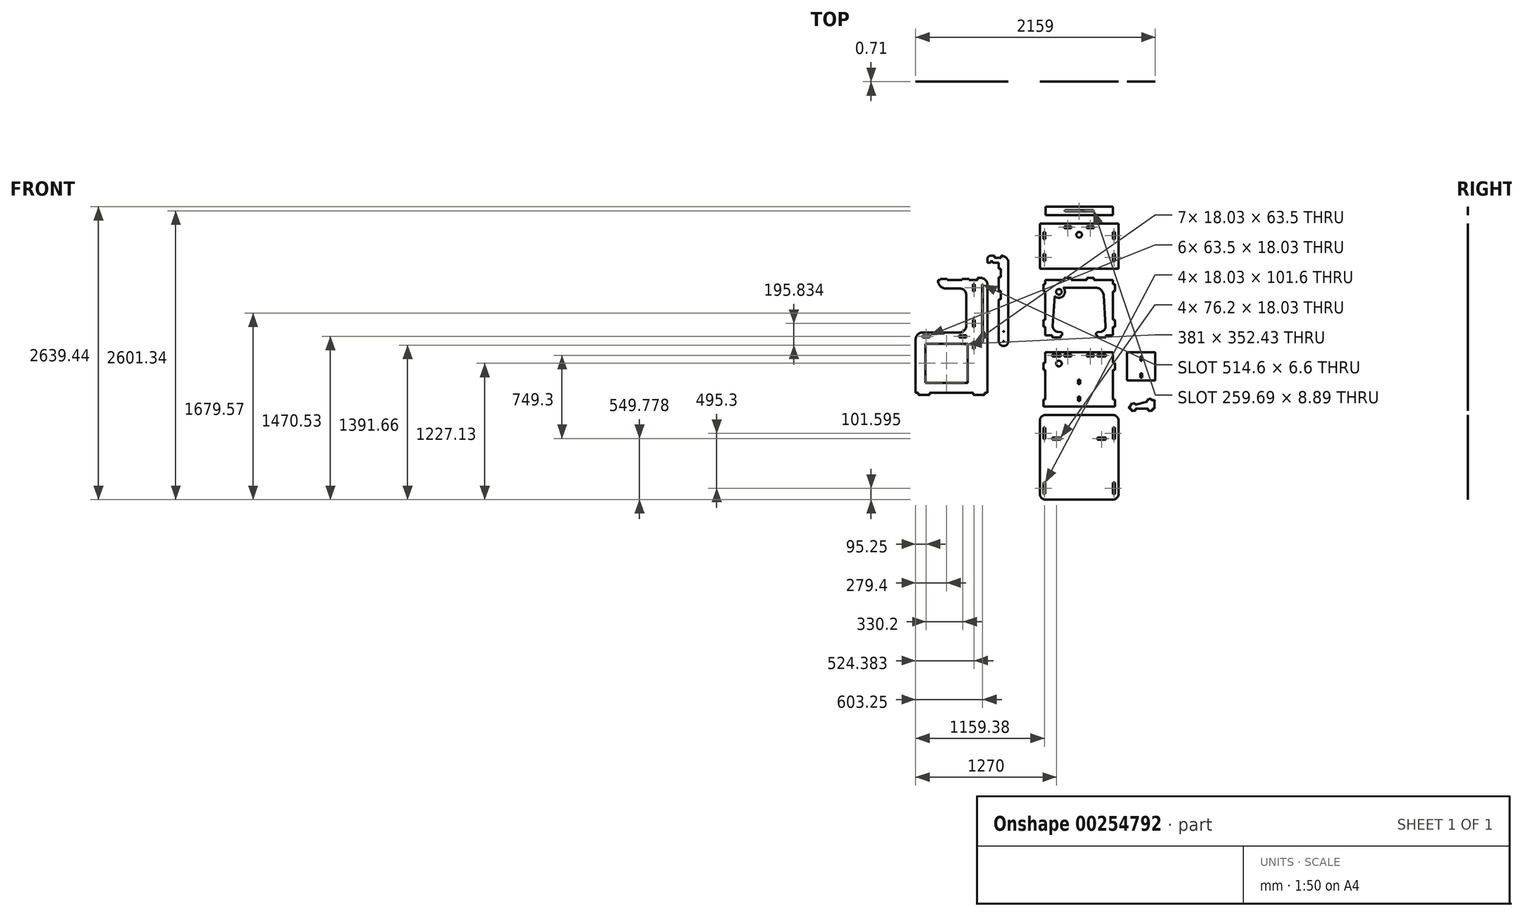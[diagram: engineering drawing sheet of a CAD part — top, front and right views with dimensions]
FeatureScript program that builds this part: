
annotation { "Feature Type Name" : "Feature", "Feature Type Description" : "" }
export const myFeature = defineFeature(function(context is Context, id is Id, definition is map)
    precondition{}
    {
        {
            assignVariable(context, id + "F0", {"name" : "ply34", "anyValue" : .71});
        }
        {
            var Q0;
            Q0=qCreatedBy(makeId("Front.planeOp"),FACE);
            var sketch = newSketch(context, id + "F1", { "sketchPlane" : qUnion([Q0])});
            skLineSegment(sketch, "E0.bottom", {"start": v(-279.4, 635) * mm, "end": v(279.4, 635) * mm, "construction": true});
            skLineSegment(sketch, "E0.top", {"start": v(-279.4, -635) * mm, "end": v(279.4, -635) * mm});
            skPoint(sketch, "E0.middle", {"position": v(0, 0) * mm});
            skLineSegment(sketch, "E1", {"start": v(0, 869.95) * mm, "end": v(0, 400.05) * mm, "construction": true});
            skPoint(sketch, "E1.endSnap0", {"position": v(0, 635) * mm});
            skLineSegment(sketch, "E2", {"start": v(279.4, -635) * mm, "end": v(279.4, -482.6) * mm, "construction": true});
            skLineSegment(sketch, "E3", {"start": v(279.4, 400.05) * mm, "end": v(304.8, 400.05) * mm});
            skLineSegment(sketch, "E4", {"start": v(368.3, 336.55) * mm, "end": v(368.3, -635) * mm});
            skLineSegment(sketch, "E5", {"start": v(323.85, -234.95) * mm, "end": v(323.85, -234.95) * mm});
            skLineSegment(sketch, "E6", {"start": v(279.4, 382.02) * mm, "end": v(-76.2, 382.02) * mm});
            skLineSegment(sketch, "E7", {"start": v(-76.2, 382.02) * mm, "end": v(-76.2, 369.32) * mm});
            skLineSegment(sketch, "E8", {"start": v(-12.7, 305.82) * mm, "end": v(114.3, 305.82) * mm});
            skLineSegment(sketch, "E9", {"start": v(177.8, 242.32) * mm, "end": v(177.8, -28.57) * mm});
            skLineSegment(sketch, "E10", {"start": v(114.3, -92.07) * mm, "end": v(-215.9, -92.08) * mm});
            skPoint(sketch, "E11", {"position": v(279.4, -117.47) * mm});
            skLineSegment(sketch, "E12", {"start": v(-279.4, -155.58) * mm, "end": v(-279.4, -635) * mm});
            skLineSegment(sketch, "E13", {"start": v(-57.15, 382.02) * mm, "end": v(-57.15, 391.03) * mm});
            skLineSegment(sketch, "E14", {"start": v(-57.15, 391.03) * mm, "end": v(6.35, 391.03) * mm});
            skLineSegment(sketch, "E15", {"start": v(6.35, 391.03) * mm, "end": v(6.35, 382.02) * mm});
            skLineSegment(sketch, "E16", {"start": v(139.7, 382.02) * mm, "end": v(139.7, 391.03) * mm});
            skLineSegment(sketch, "E17", {"start": v(139.7, 391.03) * mm, "end": v(203.2, 391.03) * mm});
            skLineSegment(sketch, "E18", {"start": v(203.2, 391.03) * mm, "end": v(203.2, 382.02) * mm});
            skPoint(sketch, "E19.visualSharp", {"position": v(-76.2, 305.82) * mm});
            skArc(sketch, "E19.filletArc", {"start": v(-76.2, 369.32) * mm, "mid": v(-57.6, 324.41) * mm, "end": v(-12.7, 305.82) * mm});
            skPoint(sketch, "E20.visualSharp", {"position": v(177.8, 305.82) * mm});
            skArc(sketch, "E20.filletArc", {"start": v(177.8, 242.32) * mm, "mid": v(159.2, 287.22) * mm, "end": v(114.3, 305.82) * mm});
            skPoint(sketch, "E21.visualSharp", {"position": v(177.8, -92.07) * mm});
            skArc(sketch, "E21.filletArc", {"start": v(114.3, -92.08) * mm, "mid": v(159.2, -73.48) * mm, "end": v(177.8, -28.57) * mm});
            skPoint(sketch, "E22.visualSharp", {"position": v(-279.4, -92.08) * mm});
            skArc(sketch, "E22.filletArc", {"start": v(-215.9, -92.08) * mm, "mid": v(-260.8, -110.67) * mm, "end": v(-279.4, -155.58) * mm});
            skPoint(sketch, "E23.visualSharp", {"position": v(368.3, 400.05) * mm});
            skArc(sketch, "E23.filletArc", {"start": v(368.3, 336.55) * mm, "mid": v(349.7, 381.45) * mm, "end": v(304.8, 400.05) * mm});
            skLineSegment(sketch, "E24", {"start": v(279.4, -234.95) * mm, "end": v(279.4, 400.05) * mm, "construction": true});
            skLineSegment(sketch, "E25", {"start": v(279.4, 400.05) * mm, "end": v(279.4, 382.02) * mm});
            skLineSegment(sketch, "E26.bottom", {"start": v(-215.9, -117.47) * mm, "end": v(-152.4, -117.47) * mm});
            skLineSegment(sketch, "E26.top", {"start": v(-215.9, -135.5) * mm, "end": v(-152.4, -135.5) * mm});
            skLineSegment(sketch, "E26.left", {"start": v(-215.9, -117.47) * mm, "end": v(-215.9, -135.5) * mm});
            skLineSegment(sketch, "E26.right", {"start": v(-152.4, -117.47) * mm, "end": v(-152.4, -135.5) * mm});
            skLineSegment(sketch, "E27.bottom", {"start": v(177.8, -117.47) * mm, "end": v(114.3, -117.47) * mm});
            skLineSegment(sketch, "E27.top", {"start": v(177.8, -135.5) * mm, "end": v(114.3, -135.5) * mm});
            skLineSegment(sketch, "E27.left", {"start": v(177.8, -117.48) * mm, "end": v(177.8, -135.5) * mm});
            skLineSegment(sketch, "E27.right", {"start": v(114.3, -117.48) * mm, "end": v(114.3, -135.5) * mm});
            skLineSegment(sketch, "E28", {"start": v(279.4, 82.55) * mm, "end": v(368.3, 82.55) * mm, "construction": true});
            skLineSegment(sketch, "E29", {"start": v(323.85, 336.55) * mm, "end": v(323.85, -171.45) * mm});
            skPoint(sketch, "E29.startSnap0", {"position": v(323.85, 82.55) * mm});
            skPoint(sketch, "E30.visualSharp", {"position": v(368.3, -234.95) * mm});
            skPoint(sketch, "E31.visualSharp", {"position": v(279.4, -234.95) * mm});
            skArc(sketch, "E32.0.startCap", {"start": v(320.55, 336.55) * mm, "mid": v(323.85, 339.85) * mm, "end": v(327.15, 336.55) * mm});
            skArc(sketch, "E32.0.endCap", {"start": v(327.15, -171.45) * mm, "mid": v(323.85, -174.75) * mm, "end": v(320.55, -171.45) * mm});
            skLineSegment(sketch, "E32.0.left", {"start": v(327.15, 336.55) * mm, "end": v(327.15, -171.45) * mm});
            skLineSegment(sketch, "E32.0.right", {"start": v(320.55, 336.55) * mm, "end": v(320.55, -171.45) * mm});
            skLineSegment(sketch, "E33.0", {"start": v(190.5, -546.1) * mm, "end": v(190.5, -193.68) * mm});
            skLineSegment(sketch, "E33.1", {"start": v(-190.5, -546.1) * mm, "end": v(190.5, -546.1) * mm});
            skLineSegment(sketch, "E33.2", {"start": v(-190.5, -193.68) * mm, "end": v(-190.5, -546.1) * mm});
            skLineSegment(sketch, "E34", {"start": v(-190.5, -193.68) * mm, "end": v(190.5, -193.67) * mm});
            skLineSegment(sketch, "E35.bottom", {"start": v(254, 343.92) * mm, "end": v(235.97, 343.92) * mm});
            skLineSegment(sketch, "E35.top", {"start": v(254, 280.42) * mm, "end": v(235.97, 280.42) * mm});
            skLineSegment(sketch, "E35.left", {"start": v(254, 343.92) * mm, "end": v(254, 280.42) * mm});
            skLineSegment(sketch, "E35.right", {"start": v(235.97, 343.92) * mm, "end": v(235.97, 280.42) * mm});
            skLineSegment(sketch, "E36.bottom", {"start": v(235.97, 22.23) * mm, "end": v(254, 22.23) * mm});
            skLineSegment(sketch, "E36.top", {"start": v(235.97, -41.27) * mm, "end": v(254, -41.27) * mm});
            skLineSegment(sketch, "E36.left", {"start": v(235.97, 22.22) * mm, "end": v(235.97, -41.28) * mm});
            skLineSegment(sketch, "E36.right", {"start": v(254, 22.22) * mm, "end": v(254, -41.28) * mm});
            skLineSegment(sketch, "E37", {"start": v(889, -117.47) * mm, "end": v(1498.6, -117.47) * mm, "construction": true});
            skLineSegment(sketch, "E38", {"start": v(1041.4, -117.47) * mm, "end": v(1041.4, -103.09) * mm});
            skLineSegment(sketch, "E39", {"start": v(1193.8, -117.47) * mm, "end": v(1193.8, 9.53) * mm, "construction": true});
            skLineSegment(sketch, "E40", {"start": v(1030.5, -90.52) * mm, "end": v(999.05, -86.03) * mm});
            skLineSegment(sketch, "E41", {"start": v(955.54, -32.45) * mm, "end": v(973.28, 240.9) * mm});
            skPoint(sketch, "E41.endSnap0", {"position": v(254, 312.17) * mm});
            skPoint(sketch, "E42.visualSharp", {"position": v(1041.4, -92.07) * mm});
            skArc(sketch, "E42.filletArc", {"start": v(1041.4, -103.09) * mm, "mid": v(1038.3, -94.77) * mm, "end": v(1030.5, -90.52) * mm});
            skPoint(sketch, "E43.visualSharp", {"position": v(952.5, -79.37) * mm});
            skArc(sketch, "E43.filletArc", {"start": v(955.54, -32.45) * mm, "mid": v(966.8, -67.76) * mm, "end": v(999.05, -86.03) * mm});
            skLineSegment(sketch, "E44", {"start": v(889, -117.47) * mm, "end": v(889, 382.02) * mm});
            skLineSegment(sketch, "E45", {"start": v(1041.4, -117.47) * mm, "end": v(889, -117.47) * mm});
            skLineSegment(sketch, "E46", {"start": v(1028.7, -117.47) * mm, "end": v(1028.7, -135.5) * mm});
            skLineSegment(sketch, "E47", {"start": v(1028.7, -135.5) * mm, "end": v(952.5, -135.5) * mm});
            skLineSegment(sketch, "E48", {"start": v(952.5, -135.5) * mm, "end": v(952.5, -117.47) * mm});
            skLineSegment(sketch, "E49.MirrorCS", {"start": v(1432.06, -32.45) * mm, "end": v(1414.32, 240.9) * mm});
            skLineSegment(sketch, "E50.MirrorCS", {"start": v(1498.6, -117.47) * mm, "end": v(1498.6, 382.02) * mm});
            skArc(sketch, "E51.MirrorCS", {"start": v(1432.06, -32.45) * mm, "mid": v(1420.8, -67.76) * mm, "end": v(1388.55, -86.03) * mm});
            skLineSegment(sketch, "E52.MirrorCS", {"start": v(1357.1, -90.52) * mm, "end": v(1388.55, -86.03) * mm});
            skArc(sketch, "E53.MirrorCS", {"start": v(1346.2, -103.09) * mm, "mid": v(1349.3, -94.77) * mm, "end": v(1357.1, -90.52) * mm});
            skLineSegment(sketch, "E54.MirrorCS", {"start": v(1346.2, -117.47) * mm, "end": v(1346.2, -103.09) * mm});
            skLineSegment(sketch, "E55.MirrorCS", {"start": v(1435.1, -135.5) * mm, "end": v(1435.1, -117.47) * mm});
            skLineSegment(sketch, "E56.MirrorCS", {"start": v(1358.9, -135.5) * mm, "end": v(1435.1, -135.5) * mm});
            skLineSegment(sketch, "E57.MirrorCS", {"start": v(1346.2, -117.48) * mm, "end": v(1498.6, -117.48) * mm});
            skLineSegment(sketch, "E58.MirrorCS", {"start": v(1358.9, -117.47) * mm, "end": v(1358.9, -135.5) * mm});
            skLineSegment(sketch, "E59", {"start": v(1049.32, 312.17) * mm, "end": v(1338.28, 312.17) * mm});
            skPoint(sketch, "E60.visualSharp", {"position": v(977.9, 312.17) * mm});
            skArc(sketch, "E60.filletArc", {"start": v(1049.32, 312.17) * mm, "mid": v(997.2, 291.56) * mm, "end": v(973.28, 240.9) * mm});
            skPoint(sketch, "E61.visualSharp", {"position": v(1409.7, 312.17) * mm});
            skArc(sketch, "E61.filletArc", {"start": v(1414.32, 240.9) * mm, "mid": v(1390.4, 291.56) * mm, "end": v(1338.28, 312.17) * mm});
            skLineSegment(sketch, "E62", {"start": v(889, 382.02) * mm, "end": v(1498.6, 382.02) * mm});
            skLineSegment(sketch, "E63", {"start": v(1060.45, 382.02) * mm, "end": v(1060.45, 400.05) * mm});
            skLineSegment(sketch, "E64", {"start": v(1060.45, 400.05) * mm, "end": v(1123.95, 400.05) * mm});
            skLineSegment(sketch, "E65", {"start": v(1123.95, 400.05) * mm, "end": v(1123.95, 382.02) * mm});
            skLineSegment(sketch, "E66", {"start": v(889, 343.92) * mm, "end": v(870.97, 343.92) * mm});
            skLineSegment(sketch, "E67", {"start": v(870.97, 343.92) * mm, "end": v(870.97, 280.42) * mm});
            skLineSegment(sketch, "E68", {"start": v(870.97, 280.42) * mm, "end": v(889, 280.42) * mm});
            skLineSegment(sketch, "E69", {"start": v(889, -41.27) * mm, "end": v(870.97, -41.27) * mm});
            skLineSegment(sketch, "E70", {"start": v(870.97, -41.27) * mm, "end": v(870.97, 22.23) * mm});
            skLineSegment(sketch, "E71", {"start": v(870.97, 22.22) * mm, "end": v(889, 22.22) * mm});
            skLineSegment(sketch, "E72.MirrorCS", {"start": v(1516.63, 22.23) * mm, "end": v(1498.6, 22.23) * mm});
            skLineSegment(sketch, "E73.MirrorCS", {"start": v(1498.6, -41.28) * mm, "end": v(1516.63, -41.28) * mm});
            skLineSegment(sketch, "E74.MirrorCS", {"start": v(1498.6, 343.92) * mm, "end": v(1516.63, 343.92) * mm});
            skLineSegment(sketch, "E75.MirrorCS", {"start": v(1516.63, 280.42) * mm, "end": v(1498.6, 280.42) * mm});
            skLineSegment(sketch, "E76.MirrorCS", {"start": v(1516.63, -41.27) * mm, "end": v(1516.63, 22.23) * mm});
            skLineSegment(sketch, "E77.MirrorCS", {"start": v(1516.63, 343.92) * mm, "end": v(1516.63, 280.42) * mm});
            skLineSegment(sketch, "E78.bottom", {"start": v(1498.6, -269.88) * mm, "end": v(889, -269.87) * mm});
            skLineSegment(sketch, "E78.top", {"start": v(1498.6, -758.83) * mm, "end": v(889, -758.83) * mm});
            skLineSegment(sketch, "E78.left", {"start": v(1498.6, -269.87) * mm, "end": v(1498.6, -758.83) * mm});
            skLineSegment(sketch, "E78.right", {"start": v(889, -269.87) * mm, "end": v(889, -758.83) * mm});
            skLineSegment(sketch, "E79", {"start": v(889, -365.12) * mm, "end": v(870.97, -365.12) * mm});
            skLineSegment(sketch, "E80", {"start": v(870.97, -365.12) * mm, "end": v(870.97, -428.63) * mm});
            skLineSegment(sketch, "E81", {"start": v(870.97, -428.63) * mm, "end": v(889, -428.63) * mm});
            skLineSegment(sketch, "E82", {"start": v(889, -695.32) * mm, "end": v(870.97, -695.32) * mm});
            skLineSegment(sketch, "E83", {"start": v(870.97, -695.32) * mm, "end": v(870.97, -758.82) * mm});
            skLineSegment(sketch, "E84", {"start": v(870.97, -758.82) * mm, "end": v(889, -758.82) * mm});
            skLineSegment(sketch, "E85.MirrorCS", {"start": v(1516.63, -758.82) * mm, "end": v(1498.6, -758.82) * mm});
            skLineSegment(sketch, "E86.MirrorCS", {"start": v(1498.6, -695.33) * mm, "end": v(1516.63, -695.33) * mm});
            skLineSegment(sketch, "E87.MirrorCS", {"start": v(1516.63, -428.62) * mm, "end": v(1498.6, -428.62) * mm});
            skLineSegment(sketch, "E88.MirrorCS", {"start": v(1498.6, -365.12) * mm, "end": v(1516.63, -365.12) * mm});
            skLineSegment(sketch, "E89.MirrorCS", {"start": v(1516.63, -695.32) * mm, "end": v(1516.63, -758.82) * mm});
            skLineSegment(sketch, "E90.MirrorCS", {"start": v(1516.63, -365.12) * mm, "end": v(1516.63, -428.63) * mm});
            skLineSegment(sketch, "E91", {"start": v(952.5, -288.93) * mm, "end": v(952.5, -306.96) * mm});
            skLineSegment(sketch, "E92", {"start": v(952.5, -306.96) * mm, "end": v(1028.7, -306.96) * mm});
            skLineSegment(sketch, "E93", {"start": v(1028.7, -306.96) * mm, "end": v(1028.7, -288.93) * mm});
            skLineSegment(sketch, "E94", {"start": v(1028.7, -288.92) * mm, "end": v(952.5, -288.92) * mm});
            skLineSegment(sketch, "E95", {"start": v(0, -635) * mm, "end": v(0, -546.1) * mm, "construction": true});
            skLineSegment(sketch, "E96", {"start": v(1600.2, 382.02) * mm, "end": v(1600.2, -117.47) * mm, "construction": true});
            skLineSegment(sketch, "E97.MirrorCS", {"start": v(1263.65, 400.05) * mm, "end": v(1263.65, 382.02) * mm});
            skLineSegment(sketch, "E98.MirrorCS", {"start": v(1327.15, 382.02) * mm, "end": v(1327.15, 400.05) * mm});
            skLineSegment(sketch, "E99.MirrorCS", {"start": v(1327.15, 400.05) * mm, "end": v(1263.65, 400.05) * mm});
            skLineSegment(sketch, "E100.MirrorCS", {"start": v(1435.1, -288.93) * mm, "end": v(1435.1, -306.96) * mm});
            skLineSegment(sketch, "E101.MirrorCS", {"start": v(1358.9, -288.93) * mm, "end": v(1435.1, -288.93) * mm});
            skLineSegment(sketch, "E102.MirrorCS", {"start": v(1358.9, -306.96) * mm, "end": v(1358.9, -288.92) * mm});
            skLineSegment(sketch, "E103.MirrorCS", {"start": v(1435.1, -306.96) * mm, "end": v(1358.9, -306.96) * mm});
            skLineSegment(sketch, "E104.bottom", {"start": v(1060.45, -288.93) * mm, "end": v(1123.95, -288.93) * mm});
            skLineSegment(sketch, "E104.top", {"start": v(1060.45, -306.96) * mm, "end": v(1123.95, -306.96) * mm});
            skLineSegment(sketch, "E104.left", {"start": v(1060.45, -288.92) * mm, "end": v(1060.45, -306.96) * mm});
            skLineSegment(sketch, "E104.right", {"start": v(1123.95, -288.92) * mm, "end": v(1123.95, -306.96) * mm});
            skLineSegment(sketch, "E105.bottom", {"start": v(1263.65, -288.93) * mm, "end": v(1327.15, -288.93) * mm});
            skLineSegment(sketch, "E105.top", {"start": v(1263.65, -306.96) * mm, "end": v(1327.15, -306.96) * mm});
            skLineSegment(sketch, "E105.left", {"start": v(1263.65, -288.92) * mm, "end": v(1263.65, -306.96) * mm});
            skLineSegment(sketch, "E105.right", {"start": v(1327.15, -288.92) * mm, "end": v(1327.15, -306.96) * mm});
            skLineSegment(sketch, "E106.bottom", {"start": v(235.97, -173.6) * mm, "end": v(254, -173.6) * mm});
            skLineSegment(sketch, "E106.top", {"start": v(235.97, -237.1) * mm, "end": v(254, -237.1) * mm});
            skLineSegment(sketch, "E106.left", {"start": v(235.97, -173.6) * mm, "end": v(235.97, -237.1) * mm});
            skLineSegment(sketch, "E106.right", {"start": v(254, -173.6) * mm, "end": v(254, -237.1) * mm});
            skLineSegment(sketch, "E107.bottom", {"start": v(235.97, -676.27) * mm, "end": v(254, -676.27) * mm});
            skLineSegment(sketch, "E107.top", {"start": v(235.97, -739.77) * mm, "end": v(254, -739.77) * mm});
            skLineSegment(sketch, "E107.left", {"start": v(235.97, -676.27) * mm, "end": v(235.97, -739.77) * mm});
            skLineSegment(sketch, "E107.right", {"start": v(254, -676.27) * mm, "end": v(254, -739.77) * mm});
            skLineSegment(sketch, "E108.bottom", {"start": v(890.02, -835.03) * mm, "end": v(1497.58, -835.03) * mm});
            skLineSegment(sketch, "E108.top", {"start": v(890.02, -1597.03) * mm, "end": v(1497.58, -1597.03) * mm});
            skLineSegment(sketch, "E108.left", {"start": v(839.22, -885.83) * mm, "end": v(839.22, -1546.23) * mm});
            skLineSegment(sketch, "E108.right", {"start": v(1548.38, -885.83) * mm, "end": v(1548.38, -1546.23) * mm});
            skPoint(sketch, "E109.visualSharp", {"position": v(839.22, -835.03) * mm});
            skArc(sketch, "E109.filletArc", {"start": v(890.02, -835.03) * mm, "mid": v(854.1, -849.9) * mm, "end": v(839.22, -885.83) * mm});
            skPoint(sketch, "E110.visualSharp", {"position": v(1548.38, -835.03) * mm});
            skArc(sketch, "E110.filletArc", {"start": v(1548.38, -885.83) * mm, "mid": v(1533.5, -849.9) * mm, "end": v(1497.58, -835.03) * mm});
            skPoint(sketch, "E111.visualSharp", {"position": v(1548.38, -1597.03) * mm});
            skArc(sketch, "E111.filletArc", {"start": v(1497.58, -1597.03) * mm, "mid": v(1533.5, -1582.15) * mm, "end": v(1548.38, -1546.23) * mm});
            skPoint(sketch, "E112.visualSharp", {"position": v(839.22, -1597.03) * mm});
            skArc(sketch, "E112.filletArc", {"start": v(839.22, -1546.23) * mm, "mid": v(854.1, -1582.15) * mm, "end": v(890.02, -1597.03) * mm});
            skLineSegment(sketch, "E113.bottom", {"start": v(870.97, -949.33) * mm, "end": v(889, -949.33) * mm});
            skLineSegment(sketch, "E113.top", {"start": v(870.97, -1050.93) * mm, "end": v(889, -1050.93) * mm});
            skLineSegment(sketch, "E113.left", {"start": v(870.97, -949.33) * mm, "end": v(870.97, -1050.93) * mm});
            skLineSegment(sketch, "E113.right", {"start": v(889, -949.33) * mm, "end": v(889, -1050.93) * mm});
            skLineSegment(sketch, "E114.bottom", {"start": v(870.97, -1546.23) * mm, "end": v(889, -1546.23) * mm});
            skLineSegment(sketch, "E114.top", {"start": v(870.97, -1444.63) * mm, "end": v(889, -1444.63) * mm});
            skLineSegment(sketch, "E114.left", {"start": v(870.97, -1546.23) * mm, "end": v(870.97, -1444.63) * mm});
            skLineSegment(sketch, "E114.right", {"start": v(889, -1546.23) * mm, "end": v(889, -1444.63) * mm});
            skLineSegment(sketch, "E115", {"start": v(889, -1050.93) * mm, "end": v(889, -1444.63) * mm, "construction": true});
            skPoint(sketch, "E116", {"position": v(1193.8, -1216.03) * mm});
            skPoint(sketch, "E117", {"position": v(839.22, -1216.03) * mm});
            skLineSegment(sketch, "E118", {"start": v(-254, -635) * mm, "end": v(-254, -653.03) * mm});
            skLineSegment(sketch, "E119", {"start": v(-254, -653.03) * mm, "end": v(-152.4, -653.03) * mm});
            skLineSegment(sketch, "E120", {"start": v(-152.4, -653.03) * mm, "end": v(-152.4, -635) * mm});
            skLineSegment(sketch, "E121.MirrorCS", {"start": v(1516.63, -949.33) * mm, "end": v(1498.6, -949.33) * mm});
            skLineSegment(sketch, "E122.MirrorCS", {"start": v(1516.63, -1444.63) * mm, "end": v(1498.6, -1444.63) * mm});
            skLineSegment(sketch, "E123.MirrorCS", {"start": v(1516.63, -1050.93) * mm, "end": v(1498.6, -1050.93) * mm});
            skLineSegment(sketch, "E124.MirrorCS", {"start": v(1516.63, -1546.23) * mm, "end": v(1498.6, -1546.23) * mm});
            skLineSegment(sketch, "E125.MirrorCS", {"start": v(1516.63, -949.33) * mm, "end": v(1516.63, -1050.93) * mm});
            skLineSegment(sketch, "E126.MirrorCS", {"start": v(1498.6, -949.33) * mm, "end": v(1498.6, -1050.93) * mm});
            skLineSegment(sketch, "E127.MirrorCS", {"start": v(1498.6, -1050.93) * mm, "end": v(1498.6, -1444.63) * mm, "construction": true});
            skLineSegment(sketch, "E128.MirrorCS", {"start": v(1498.6, -1546.23) * mm, "end": v(1498.6, -1444.63) * mm});
            skLineSegment(sketch, "E129.MirrorCS", {"start": v(1516.63, -1546.23) * mm, "end": v(1516.63, -1444.63) * mm});
            skPoint(sketch, "E130.MirrorP", {"position": v(1548.38, -1216.03) * mm});
            skLineSegment(sketch, "E131.bottom", {"start": v(952.5, -1038.23) * mm, "end": v(1028.7, -1038.23) * mm});
            skLineSegment(sketch, "E131.top", {"start": v(952.5, -1056.26) * mm, "end": v(1028.7, -1056.26) * mm});
            skLineSegment(sketch, "E131.left", {"start": v(952.5, -1038.23) * mm, "end": v(952.5, -1056.26) * mm});
            skLineSegment(sketch, "E131.right", {"start": v(1028.7, -1038.23) * mm, "end": v(1028.7, -1056.26) * mm});
            skLineSegment(sketch, "E132.bottom", {"start": v(1435.1, -1056.26) * mm, "end": v(1358.9, -1056.26) * mm});
            skLineSegment(sketch, "E132.top", {"start": v(1435.1, -1038.23) * mm, "end": v(1358.9, -1038.23) * mm});
            skLineSegment(sketch, "E132.left", {"start": v(1435.1, -1038.23) * mm, "end": v(1435.1, -1056.26) * mm});
            skLineSegment(sketch, "E132.right", {"start": v(1358.9, -1038.23) * mm, "end": v(1358.9, -1056.26) * mm});
            skLineSegment(sketch, "E133.bottom", {"start": v(839.22, 483.62) * mm, "end": v(1548.38, 483.62) * mm});
            skLineSegment(sketch, "E133.top", {"start": v(839.22, 890.02) * mm, "end": v(1548.38, 890.02) * mm});
            skLineSegment(sketch, "E133.left", {"start": v(839.22, 483.62) * mm, "end": v(839.22, 890.02) * mm});
            skLineSegment(sketch, "E133.right", {"start": v(1548.38, 483.62) * mm, "end": v(1548.38, 890.02) * mm});
            skLineSegment(sketch, "E134.bottom", {"start": v(1060.45, 864.62) * mm, "end": v(1123.95, 864.62) * mm});
            skLineSegment(sketch, "E134.top", {"start": v(1060.45, 846.58) * mm, "end": v(1123.95, 846.58) * mm});
            skLineSegment(sketch, "E134.left", {"start": v(1060.45, 864.62) * mm, "end": v(1060.45, 846.58) * mm});
            skLineSegment(sketch, "E134.right", {"start": v(1123.95, 864.62) * mm, "end": v(1123.95, 846.58) * mm});
            skLineSegment(sketch, "E135.bottom", {"start": v(1263.65, 864.62) * mm, "end": v(1327.15, 864.62) * mm});
            skLineSegment(sketch, "E135.top", {"start": v(1263.65, 846.58) * mm, "end": v(1327.15, 846.58) * mm});
            skLineSegment(sketch, "E135.left", {"start": v(1263.65, 864.62) * mm, "end": v(1263.65, 846.58) * mm});
            skLineSegment(sketch, "E135.right", {"start": v(1327.15, 864.62) * mm, "end": v(1327.15, 846.58) * mm});
            skLineSegment(sketch, "E136.bottom", {"start": v(870.97, 813.82) * mm, "end": v(889, 813.82) * mm});
            skLineSegment(sketch, "E136.top", {"start": v(870.97, 750.32) * mm, "end": v(889, 750.32) * mm});
            skLineSegment(sketch, "E136.left", {"start": v(870.97, 813.82) * mm, "end": v(870.97, 750.32) * mm});
            skLineSegment(sketch, "E136.right", {"start": v(889, 813.82) * mm, "end": v(889, 750.32) * mm});
            skLineSegment(sketch, "E137.bottom", {"start": v(870.97, 616.97) * mm, "end": v(889, 616.97) * mm});
            skLineSegment(sketch, "E137.top", {"start": v(870.97, 553.47) * mm, "end": v(889, 553.47) * mm});
            skLineSegment(sketch, "E137.left", {"start": v(870.97, 616.97) * mm, "end": v(870.97, 553.47) * mm});
            skLineSegment(sketch, "E137.right", {"start": v(889, 616.97) * mm, "end": v(889, 553.47) * mm});
            skLineSegment(sketch, "E138.MirrorCS", {"start": v(1516.63, 813.82) * mm, "end": v(1498.6, 813.82) * mm});
            skLineSegment(sketch, "E139.MirrorCS", {"start": v(1516.63, 616.97) * mm, "end": v(1498.6, 616.97) * mm});
            skLineSegment(sketch, "E140.MirrorCS", {"start": v(1516.63, 750.32) * mm, "end": v(1498.6, 750.32) * mm});
            skLineSegment(sketch, "E141.MirrorCS", {"start": v(1516.63, 553.47) * mm, "end": v(1498.6, 553.47) * mm});
            skLineSegment(sketch, "E142.MirrorCS", {"start": v(1498.6, 616.97) * mm, "end": v(1498.6, 553.47) * mm});
            skLineSegment(sketch, "E143.MirrorCS", {"start": v(1516.63, 616.97) * mm, "end": v(1516.63, 553.47) * mm});
            skLineSegment(sketch, "E144.MirrorCS", {"start": v(1498.6, 813.82) * mm, "end": v(1498.6, 750.32) * mm});
            skLineSegment(sketch, "E145.MirrorCS", {"start": v(1516.63, 813.82) * mm, "end": v(1516.63, 750.32) * mm});
            skCircle(sketch, "E146", {"center": v(1011.3, 274.07) * mm, "radius": 25.4 * mm});
            skLineSegment(sketch, "E147", {"start": v(1049.32, 312.17) * mm, "end": v(1049.32, 235.97) * mm, "construction": true});
            skPoint(sketch, "E148", {"position": v(1049.32, 274.07) * mm});
            skLineSegment(sketch, "E149", {"start": v(1049.32, 235.97) * mm, "end": v(973.28, 235.97) * mm, "construction": true});
            skPoint(sketch, "E150", {"position": v(1011.3, 235.97) * mm});
            skArc(sketch, "E151", {"start": v(972.98, 236.27) * mm, "mid": v(1049.25, 235.9) * mm, "end": v(1049.32, 312.17) * mm});
            skLineSegment(sketch, "E152", {"start": v(368.3, -635) * mm, "end": v(279.4, -635) * mm});
            skLineSegment(sketch, "E153", {"start": v(342.9, -635) * mm, "end": v(342.9, -653.03) * mm});
            skLineSegment(sketch, "E154", {"start": v(342.9, -653.03) * mm, "end": v(241.3, -653.03) * mm});
            skLineSegment(sketch, "E155", {"start": v(241.3, -653.03) * mm, "end": v(241.3, -635) * mm});
            skLineSegment(sketch, "E156.bottom", {"start": v(511.81, -213.36) * mm, "end": v(514.35, -213.36) * mm});
            skLineSegment(sketch, "E156.top", {"start": v(469.9, 555) * mm, "end": v(556.26, 555) * mm, "construction": true});
            skLineSegment(sketch, "E156.left", {"start": v(469.9, -171.45) * mm, "end": v(469.9, 555) * mm});
            skLineSegment(sketch, "E156.right", {"start": v(556.26, -171.45) * mm, "end": v(556.26, 535.94) * mm});
            skPoint(sketch, "E157.visualSharp", {"position": v(469.9, -213.36) * mm});
            skArc(sketch, "E157.filletArc", {"start": v(469.9, -171.45) * mm, "mid": v(482.18, -201.08) * mm, "end": v(511.81, -213.36) * mm});
            skPoint(sketch, "E158.visualSharp", {"position": v(556.26, -213.36) * mm});
            skArc(sketch, "E158.filletArc", {"start": v(514.35, -213.36) * mm, "mid": v(543.98, -201.08) * mm, "end": v(556.26, -171.45) * mm});
            skLineSegment(sketch, "E159", {"start": v(513.08, -171.45) * mm, "end": v(513.08, -82.55) * mm, "construction": true});
            skPoint(sketch, "E159.startSnap0", {"position": v(513.08, -213.36) * mm});
            skCircle(sketch, "E160", {"center": v(513.08, -171.45) * mm, "radius": 3.3 * mm});
            skCircle(sketch, "E161", {"center": v(513.08, -82.55) * mm, "radius": 3.3 * mm});
            skLineSegment(sketch, "E162", {"start": v(469.9, 555) * mm, "end": v(419.1, 555) * mm, "construction": true});
            skLineSegment(sketch, "E163", {"start": v(393.7, 555) * mm, "end": v(393.7, 535.94) * mm, "construction": true});
            skLineSegment(sketch, "E164", {"start": v(393.7, 535.94) * mm, "end": v(368.3, 535.94) * mm});
            skLineSegment(sketch, "E165", {"start": v(368.3, 535.94) * mm, "end": v(368.3, 574.04) * mm});
            skLineSegment(sketch, "E166", {"start": v(393.7, 599.44) * mm, "end": v(492.76, 599.44) * mm});
            skPoint(sketch, "E167.visualSharp", {"position": v(469.9, 555) * mm});
            skPoint(sketch, "E168.visualSharp", {"position": v(556.26, 599.44) * mm});
            skArc(sketch, "E168.filletArc", {"start": v(556.26, 535.94) * mm, "mid": v(537.66, 580.84) * mm, "end": v(492.76, 599.44) * mm});
            skPoint(sketch, "E169.visualSharp", {"position": v(368.3, 599.44) * mm});
            skArc(sketch, "E169.filletArc", {"start": v(393.7, 599.44) * mm, "mid": v(375.74, 592) * mm, "end": v(368.3, 574.04) * mm});
            skPoint(sketch, "E170.visualSharp", {"position": v(393.7, 535.94) * mm});
            skPoint(sketch, "E171.visualSharp", {"position": v(368.3, 535.94) * mm});
            skPoint(sketch, "E172.visualSharp", {"position": v(393.7, 555) * mm});
            skCircle(sketch, "E173", {"center": v(1011.3, -371.48) * mm, "radius": 25.4 * mm});
            skCircle(sketch, "E174", {"center": v(1193.8, 788.42) * mm, "radius": 25.4 * mm});
            skPoint(sketch, "E174.centerSnap0", {"position": v(1193.8, 890.02) * mm});
            skLineSegment(sketch, "E175", {"start": v(419.1, 555) * mm, "end": v(419.1, 535.94) * mm, "construction": true});
            skLineSegment(sketch, "E176", {"start": v(419.1, 535.94) * mm, "end": v(469.9, 535.94) * mm});
            skLineSegment(sketch, "E177", {"start": v(419.1, 555) * mm, "end": v(393.7, 555) * mm, "construction": true});
            skLineSegment(sketch, "E178", {"start": v(406.4, 555) * mm, "end": v(393.7, 535.94) * mm});
            skLineSegment(sketch, "E179", {"start": v(406.4, 554.99) * mm, "end": v(419.1, 535.94) * mm});
            skLineSegment(sketch, "E180.bottom", {"start": v(469.9, 481.08) * mm, "end": v(487.93, 481.08) * mm});
            skLineSegment(sketch, "E180.top", {"start": v(469.9, 404.88) * mm, "end": v(487.93, 404.88) * mm});
            skLineSegment(sketch, "E180.left", {"start": v(469.9, 481.08) * mm, "end": v(469.9, 404.88) * mm});
            skLineSegment(sketch, "E180.right", {"start": v(487.93, 481.08) * mm, "end": v(487.93, 404.88) * mm});
            skPoint(sketch, "E181", {"position": v(487.93, 442.98) * mm});
            skLineSegment(sketch, "E182.bottom", {"start": v(469.9, 281.08) * mm, "end": v(487.93, 281.08) * mm});
            skLineSegment(sketch, "E182.top", {"start": v(469.9, 204.88) * mm, "end": v(487.93, 204.88) * mm});
            skLineSegment(sketch, "E182.left", {"start": v(469.9, 281.08) * mm, "end": v(469.9, 204.88) * mm});
            skLineSegment(sketch, "E182.right", {"start": v(487.93, 281.08) * mm, "end": v(487.93, 204.88) * mm});
            skPoint(sketch, "E183", {"position": v(487.93, 242.98) * mm});
            skLineSegment(sketch, "E184.bottom", {"start": v(492.76, 599.44) * mm, "end": v(429.26, 599.44) * mm});
            skLineSegment(sketch, "E184.top", {"start": v(492.76, 581.4) * mm, "end": v(429.26, 581.4) * mm});
            skLineSegment(sketch, "E184.left", {"start": v(492.76, 599.44) * mm, "end": v(492.76, 581.4) * mm});
            skLineSegment(sketch, "E184.right", {"start": v(429.26, 599.44) * mm, "end": v(429.26, 581.4) * mm});
            skLineSegment(sketch, "E185.bottom", {"start": v(1202.82, -708.03) * mm, "end": v(1184.78, -708.03) * mm});
            skLineSegment(sketch, "E185.top", {"start": v(1202.82, -669.93) * mm, "end": v(1184.78, -669.93) * mm});
            skLineSegment(sketch, "E185.left", {"start": v(1202.82, -708.03) * mm, "end": v(1202.82, -669.93) * mm});
            skLineSegment(sketch, "E185.right", {"start": v(1184.78, -708.03) * mm, "end": v(1184.78, -669.93) * mm});
            skPoint(sketch, "E185.middle", {"position": v(1193.8, -688.98) * mm});
            skPoint(sketch, "E185.middle.positionSnap0", {"position": v(1193.8, -758.83) * mm});
            skPoint(sketch, "E185.centerSnap0", {"position": v(1193.8, -758.83) * mm});
            skLineSegment(sketch, "E186.bottom", {"start": v(1202.82, -555.63) * mm, "end": v(1184.78, -555.63) * mm});
            skLineSegment(sketch, "E186.top", {"start": v(1202.82, -517.53) * mm, "end": v(1184.78, -517.53) * mm});
            skLineSegment(sketch, "E186.left", {"start": v(1202.82, -555.63) * mm, "end": v(1202.82, -517.53) * mm});
            skLineSegment(sketch, "E186.right", {"start": v(1184.78, -555.63) * mm, "end": v(1184.78, -517.53) * mm});
            skPoint(sketch, "E186.middle", {"position": v(1193.8, -536.58) * mm});
            skLineSegment(sketch, "E187", {"start": v(1643.63, -758.82) * mm, "end": v(1872.23, -697.57) * mm});
            skLineSegment(sketch, "E188", {"start": v(1872.23, -697.57) * mm, "end": v(1872.23, -777.88) * mm});
            skLineSegment(sketch, "E189", {"start": v(1643.63, -758.83) * mm, "end": v(1643.63, -777.88) * mm});
            skLineSegment(sketch, "E190", {"start": v(1643.63, -777.88) * mm, "end": v(1872.23, -777.88) * mm});
            skLineSegment(sketch, "E191", {"start": v(1662.68, -777.88) * mm, "end": v(1662.68, -795.9) * mm});
            skLineSegment(sketch, "E192", {"start": v(1662.68, -795.9) * mm, "end": v(1700.78, -795.9) * mm});
            skLineSegment(sketch, "E193", {"start": v(1700.78, -795.9) * mm, "end": v(1700.78, -777.88) * mm});
            skLineSegment(sketch, "E194", {"start": v(1815.08, -777.88) * mm, "end": v(1815.08, -795.9) * mm});
            skLineSegment(sketch, "E195", {"start": v(1815.08, -795.9) * mm, "end": v(1853.18, -795.9) * mm});
            skLineSegment(sketch, "E196", {"start": v(1853.18, -795.9) * mm, "end": v(1853.18, -777.88) * mm});
            skLineSegment(sketch, "E197", {"start": v(1662.03, -753.9) * mm, "end": v(1657.37, -736.47) * mm});
            skLineSegment(sketch, "E198", {"start": v(1657.37, -736.47) * mm, "end": v(1694.17, -726.61) * mm});
            skLineSegment(sketch, "E199", {"start": v(1694.17, -726.61) * mm, "end": v(1698.84, -744.03) * mm});
            skLineSegment(sketch, "E200", {"start": v(1809.24, -714.45) * mm, "end": v(1804.57, -697.03) * mm});
            skLineSegment(sketch, "E201", {"start": v(1804.57, -697.03) * mm, "end": v(1841.38, -687.17) * mm});
            skLineSegment(sketch, "E202", {"start": v(1841.38, -687.17) * mm, "end": v(1846.04, -704.59) * mm});
            skLineSegment(sketch, "E203.bottom", {"start": v(1879.6, -523.88) * mm, "end": v(1625.6, -523.88) * mm});
            skLineSegment(sketch, "E203.top", {"start": v(1879.6, -269.88) * mm, "end": v(1625.6, -269.88) * mm});
            skLineSegment(sketch, "E203.left", {"start": v(1879.6, -523.88) * mm, "end": v(1879.6, -269.87) * mm});
            skLineSegment(sketch, "E203.right", {"start": v(1625.6, -523.88) * mm, "end": v(1625.6, -269.88) * mm});
            skPoint(sketch, "E203.middle", {"position": v(1752.6, -396.88) * mm});
            skLineSegment(sketch, "E204.bottom", {"start": v(1761.62, -498.48) * mm, "end": v(1743.58, -498.48) * mm});
            skLineSegment(sketch, "E204.top", {"start": v(1761.62, -460.38) * mm, "end": v(1743.58, -460.38) * mm});
            skLineSegment(sketch, "E204.left", {"start": v(1761.62, -498.48) * mm, "end": v(1761.62, -460.38) * mm});
            skLineSegment(sketch, "E204.right", {"start": v(1743.58, -498.48) * mm, "end": v(1743.58, -460.38) * mm});
            skPoint(sketch, "E204.middle", {"position": v(1752.6, -479.42) * mm});
            skLineSegment(sketch, "E205.bottom", {"start": v(1761.62, -346.07) * mm, "end": v(1743.58, -346.07) * mm});
            skLineSegment(sketch, "E205.top", {"start": v(1761.62, -307.97) * mm, "end": v(1743.58, -307.97) * mm});
            skLineSegment(sketch, "E205.left", {"start": v(1761.62, -346.07) * mm, "end": v(1761.62, -307.97) * mm});
            skLineSegment(sketch, "E205.right", {"start": v(1743.58, -346.07) * mm, "end": v(1743.58, -307.97) * mm});
            skPoint(sketch, "E205.middle", {"position": v(1752.6, -327.03) * mm});
            skLineSegment(sketch, "E206.bottom", {"start": v(890.27, 966.22) * mm, "end": v(1497.33, 966.22) * mm});
            skLineSegment(sketch, "E206.top", {"start": v(890.27, 1042.42) * mm, "end": v(1497.33, 1042.42) * mm});
            skLineSegment(sketch, "E206.left", {"start": v(890.27, 966.22) * mm, "end": v(890.27, 1042.42) * mm});
            skLineSegment(sketch, "E206.right", {"start": v(1497.33, 966.22) * mm, "end": v(1497.33, 1042.42) * mm});
            skPoint(sketch, "E206.middle", {"position": v(1193.8, 1004.32) * mm});
            skLineSegment(sketch, "E207", {"start": v(1068.4, 1004.32) * mm, "end": v(1319.2, 1004.32) * mm});
            skArc(sketch, "E208.0.startCap", {"start": v(1068.4, 999.87) * mm, "mid": v(1063.96, 1004.32) * mm, "end": v(1068.4, 1008.76) * mm});
            skArc(sketch, "E208.0.endCap", {"start": v(1319.2, 1008.76) * mm, "mid": v(1323.64, 1004.32) * mm, "end": v(1319.2, 999.87) * mm});
            skLineSegment(sketch, "E208.0.left", {"start": v(1068.4, 1008.76) * mm, "end": v(1319.2, 1008.76) * mm});
            skLineSegment(sketch, "E208.0.right", {"start": v(1068.4, 999.87) * mm, "end": v(1319.2, 999.87) * mm});
            skSolve(sketch);
        }
        {
            var Q0;
            Q0=makeQuery(id+"F1.imprint","IMPRINT",FACE,{"disambiguationData":[TD([[makeQuery(id+"F1.imprint","IMPRINT",EDGE,{"derivedFrom":sQuery(id+"F1.wireOp",EDGE,"E0.top")}),1.0]])]});
            var Q1;
            {var subQ20=sQuery(id+"F1.wireOp",EDGE,"E38");Q1=makeQuery(id+"F1.imprint","IMPRINT",FACE,{"disambiguationData":[TD([[makeQuery(id+"F1.imprint","IMPRINT",EDGE,{"derivedFrom":subQ20}),1.0]])]});}
            var Q2;
            {var subQ1=sQuery(id+"F1.wireOp",EDGE,"E78.bottom");Q2=makeQuery(id+"F1.imprint","IMPRINT",FACE,{"disambiguationData":[TD([[makeQuery(id+"F1.imprint","IMPRINT",EDGE,{"derivedFrom":subQ1}),1.0]])]});}
            var Q3;
            {var subQ0=sQuery(id+"F1.wireOp",EDGE,"E13");Q3=makeQuery(id+"F1.imprint","IMPRINT",FACE,{"disambiguationData":[TD([[makeQuery(id+"F1.imprint","IMPRINT",EDGE,{"derivedFrom":subQ0}),-1.0]])]});}
            var Q4;
            {var subQ0=sQuery(id+"F1.wireOp",EDGE,"E16");Q4=makeQuery(id+"F1.imprint","IMPRINT",FACE,{"disambiguationData":[TD([[makeQuery(id+"F1.imprint","IMPRINT",EDGE,{"derivedFrom":subQ0}),-1.0]])]});}
            var Q5;
            {var subQ0=sQuery(id+"F1.wireOp",EDGE,"E63");Q5=makeQuery(id+"F1.imprint","IMPRINT",FACE,{"disambiguationData":[TD([[makeQuery(id+"F1.imprint","IMPRINT",EDGE,{"derivedFrom":subQ0}),-1.0]])]});}
            var Q6;
            {var subQ0=sQuery(id+"F1.wireOp",EDGE,"E66");Q6=makeQuery(id+"F1.imprint","IMPRINT",FACE,{"disambiguationData":[TD([[makeQuery(id+"F1.imprint","IMPRINT",EDGE,{"derivedFrom":subQ0}),1.0]])]});}
            var Q7;
            {var subQ0=sQuery(id+"F1.wireOp",EDGE,"E69");Q7=makeQuery(id+"F1.imprint","IMPRINT",FACE,{"disambiguationData":[TD([[makeQuery(id+"F1.imprint","IMPRINT",EDGE,{"derivedFrom":subQ0}),-1.0]])]});}
            var Q8;
            {var subQ0=sQuery(id+"F1.wireOp",EDGE,"E72.MirrorCS");Q8=makeQuery(id+"F1.imprint","IMPRINT",FACE,{"disambiguationData":[TD([[makeQuery(id+"F1.imprint","IMPRINT",EDGE,{"derivedFrom":subQ0}),1.0]])]});}
            var Q9;
            {var subQ0=sQuery(id+"F1.wireOp",EDGE,"E55.MirrorCS");Q9=makeQuery(id+"F1.imprint","IMPRINT",FACE,{"disambiguationData":[TD([[makeQuery(id+"F1.imprint","IMPRINT",EDGE,{"derivedFrom":subQ0}),1.0]])]});}
            var Q10;
            {var subQ0=sQuery(id+"F1.wireOp",EDGE,"E46");Q10=makeQuery(id+"F1.imprint","IMPRINT",FACE,{"disambiguationData":[TD([[makeQuery(id+"F1.imprint","IMPRINT",EDGE,{"derivedFrom":subQ0}),-1.0]])]});}
            var Q11;
            {var subQ0=sQuery(id+"F1.wireOp",EDGE,"E74.MirrorCS");Q11=makeQuery(id+"F1.imprint","IMPRINT",FACE,{"disambiguationData":[TD([[makeQuery(id+"F1.imprint","IMPRINT",EDGE,{"derivedFrom":subQ0}),-1.0]])]});}
            var Q12;
            {var subQ0=sQuery(id+"F1.wireOp",EDGE,"39a7ba81-f663-4b78-84e7-ead2885884b40.MirrorCS");Q12=makeQuery(id+"F1.imprint","IMPRINT",FACE,{"disambiguationData":[TD([[makeQuery(id+"F1.imprint","IMPRINT",EDGE,{"derivedFrom":subQ0}),1.0]])]});}
            var Q13;
            {var subQ0=sQuery(id+"F1.wireOp",EDGE,"E85.MirrorCS");Q13=makeQuery(id+"F1.imprint","IMPRINT",FACE,{"disambiguationData":[TD([[makeQuery(id+"F1.imprint","IMPRINT",EDGE,{"derivedFrom":subQ0}),-1.0]])]});}
            var Q14;
            {var subQ0=sQuery(id+"F1.wireOp",EDGE,"E87.MirrorCS");Q14=makeQuery(id+"F1.imprint","IMPRINT",FACE,{"disambiguationData":[TD([[makeQuery(id+"F1.imprint","IMPRINT",EDGE,{"derivedFrom":subQ0}),-1.0]])]});}
            var Q15;
            {var subQ0=sQuery(id+"F1.wireOp",EDGE,"E79");Q15=makeQuery(id+"F1.imprint","IMPRINT",FACE,{"disambiguationData":[TD([[makeQuery(id+"F1.imprint","IMPRINT",EDGE,{"derivedFrom":subQ0}),1.0]])]});}
            var Q16;
            {var subQ2=sQuery(id+"F1.wireOp",EDGE,"E82");Q16=makeQuery(id+"F1.imprint","IMPRINT",FACE,{"disambiguationData":[TD([[makeQuery(id+"F1.imprint","IMPRINT",EDGE,{"derivedFrom":subQ2}),1.0]])]});}
            var Q17;
            {var subQ0=sQuery(id+"F1.wireOp",EDGE,"E97.MirrorCS");Q17=makeQuery(id+"F1.imprint","IMPRINT",FACE,{"disambiguationData":[TD([[makeQuery(id+"F1.imprint","IMPRINT",EDGE,{"derivedFrom":subQ0}),1.0]])]});}
            var Q18;
            Q18=makeQuery(id+"F1.imprint","IMPRINT",FACE,{"disambiguationData":[TD([[makeQuery(id+"F1.imprint","IMPRINT",EDGE,{"derivedFrom":sQuery(id+"F1.wireOp",EDGE,"E108.bottom")}),-1.0]])]});
            var Q19;
            {var subQ0=sQuery(id+"F1.wireOp",EDGE,"E118");Q19=makeQuery(id+"F1.imprint","IMPRINT",FACE,{"disambiguationData":[TD([[makeQuery(id+"F1.imprint","IMPRINT",EDGE,{"derivedFrom":subQ0}),1.0]])]});}
            var Q20;
            {var subQ0=sQuery(id+"F1.wireOp",EDGE,"72dbb754-bb88-4eec-963b-265a9b65b4710.MirrorCS");Q20=makeQuery(id+"F1.imprint","IMPRINT",FACE,{"disambiguationData":[TD([[makeQuery(id+"F1.imprint","IMPRINT",EDGE,{"derivedFrom":subQ0}),-1.0]])]});}
            var Q21;
            Q21=makeQuery(id+"F1.imprint","IMPRINT",FACE,{"disambiguationData":[TD([[makeQuery(id+"F1.imprint","IMPRINT",EDGE,{"derivedFrom":sQuery(id+"F1.wireOp",EDGE,"E133.bottom")}),1.0]])]});
            var Q22;
            {var subQ6=sQuery(id+"F1.wireOp",EDGE,"E151");Q22=makeQuery(id+"F1.imprint","IMPRINT",FACE,{"disambiguationData":[TD([[makeQuery(id+"F1.imprint","IMPRINT",EDGE,{"derivedFrom":subQ6}),1.0]])]});}
            var Q23;
            {var subQ0=sQuery(id+"F1.wireOp",EDGE,"E153");Q23=makeQuery(id+"F1.imprint","IMPRINT",FACE,{"disambiguationData":[TD([[makeQuery(id+"F1.imprint","IMPRINT",EDGE,{"derivedFrom":subQ0}),-1.0]])]});}
            var Q24;
            Q24=makeQuery(id+"F1.imprint","IMPRINT",FACE,{"disambiguationData":[TD([[makeQuery(id+"F1.imprint","IMPRINT",EDGE,{"derivedFrom":sQuery(id+"F1.wireOp",EDGE,"E156.bottom")}),1.0]])]});
            var Q25;
            Q25=makeQuery(id+"F1.imprint","IMPRINT",FACE,{"disambiguationData":[TD([[makeQuery(id+"F1.imprint","IMPRINT",EDGE,{"derivedFrom":sQuery(id+"F1.wireOp",EDGE,"E206.bottom")}),1.0]])]});
            var Q26;
            Q26=makeQuery(id+"F1.imprint","IMPRINT",FACE,{"disambiguationData":[TD([[makeQuery(id+"F1.imprint","IMPRINT",EDGE,{"derivedFrom":sQuery(id+"F1.wireOp",EDGE,"E203.bottom")}),-1.0]])]});
            var Q27;
            {var subQ9=sQuery(id+"F1.wireOp",EDGE,"E188");Q27=makeQuery(id+"F1.imprint","IMPRINT",FACE,{"disambiguationData":[TD([[makeQuery(id+"F1.imprint","IMPRINT",EDGE,{"derivedFrom":subQ9}),-1.0]])]});}
            var Q28;
            {var subQ0=sQuery(id+"F1.wireOp",EDGE,"E197");Q28=makeQuery(id+"F1.imprint","IMPRINT",FACE,{"disambiguationData":[TD([[makeQuery(id+"F1.imprint","IMPRINT",EDGE,{"derivedFrom":subQ0}),-1.0]])]});}
            var Q29;
            {var subQ0=sQuery(id+"F1.wireOp",EDGE,"E191");Q29=makeQuery(id+"F1.imprint","IMPRINT",FACE,{"disambiguationData":[TD([[makeQuery(id+"F1.imprint","IMPRINT",EDGE,{"derivedFrom":subQ0}),1.0]])]});}
            var Q30;
            {var subQ0=sQuery(id+"F1.wireOp",EDGE,"E194");Q30=makeQuery(id+"F1.imprint","IMPRINT",FACE,{"disambiguationData":[TD([[makeQuery(id+"F1.imprint","IMPRINT",EDGE,{"derivedFrom":subQ0}),1.0]])]});}
            var Q31;
            {var subQ0=sQuery(id+"F1.wireOp",EDGE,"E200");Q31=makeQuery(id+"F1.imprint","IMPRINT",FACE,{"disambiguationData":[TD([[makeQuery(id+"F1.imprint","IMPRINT",EDGE,{"derivedFrom":subQ0}),-1.0]])]});}
            extrude(context, id + "F2", {"entities" : qUnion([Q0, Q1, Q2, Q3, Q4, Q5, Q6, Q7, Q8, Q9, Q10, Q11, Q12, Q13, Q14, Q15, Q16, Q17, Q18, Q19, Q20, Q21, Q22, Q23, Q24, Q25, Q26, Q27, Q28, Q29, Q30, Q31]), "depth" : (getVariable(context, 'ply34')) * mm});
        }
    });
